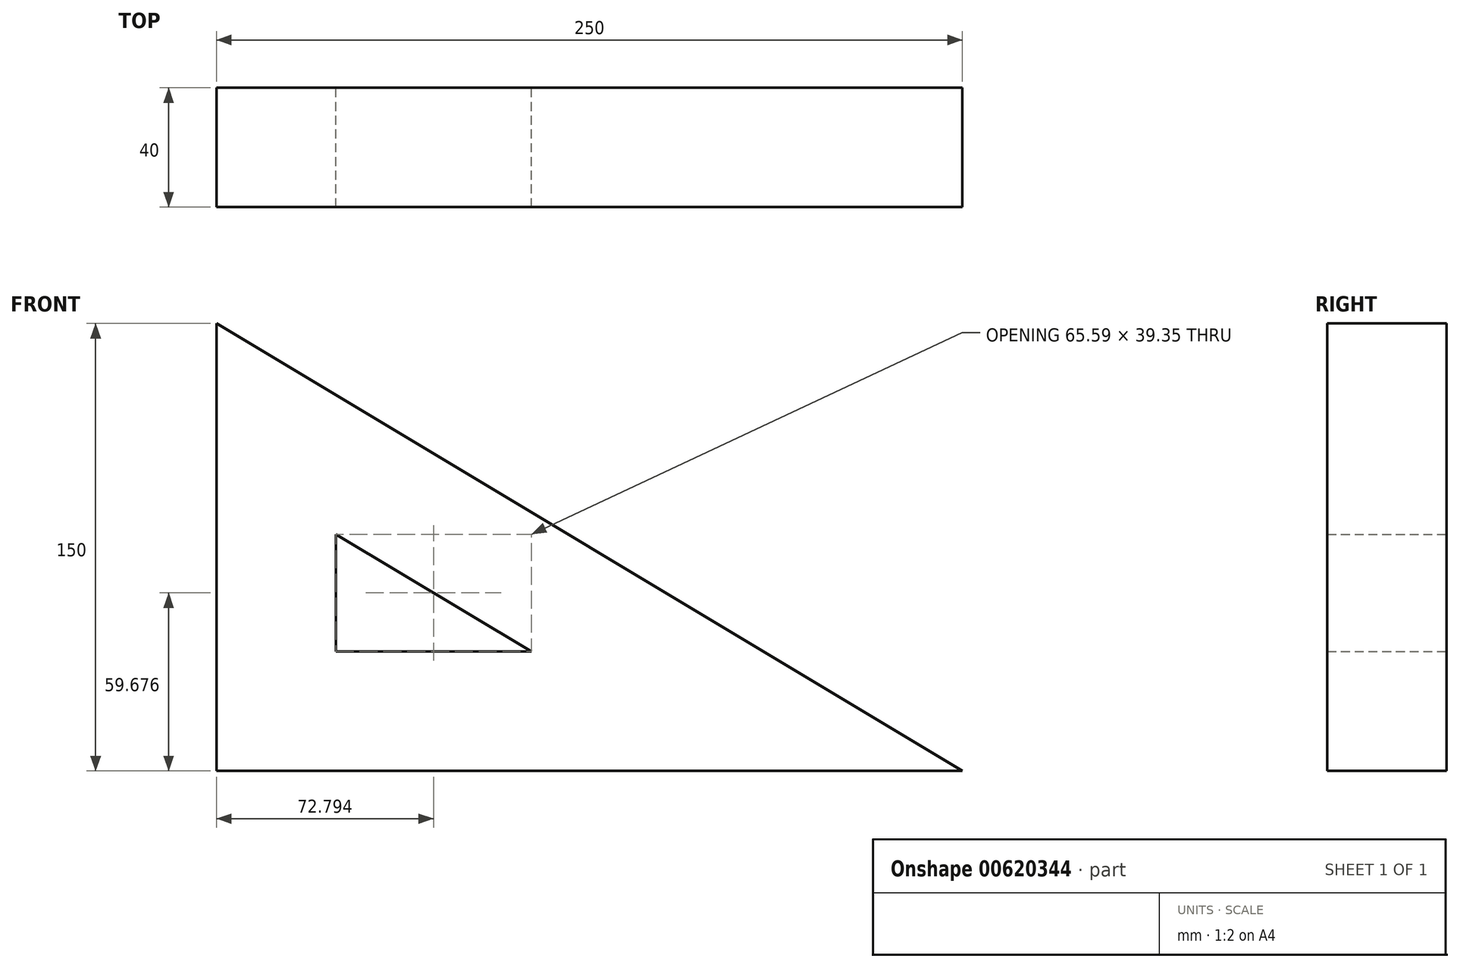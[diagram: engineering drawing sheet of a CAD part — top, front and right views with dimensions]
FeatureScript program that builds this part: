
annotation { "Feature Type Name" : "Feature", "Feature Type Description" : "" }
export const myFeature = defineFeature(function(context is Context, id is Id, definition is map)
    precondition{}
    {
        {
            var Q0;
            Q0=qCreatedBy(makeId("Front.planeOp"),FACE);
            var sketch = newSketch(context, id + "F0", { "sketchPlane" : qUnion([Q0])});
            skLineSegment(sketch, "E0", {"start": v(0, 0) * mm, "end": v(0, 150) * mm});
            skLineSegment(sketch, "E1", {"start": v(0, 150) * mm, "end": v(250, 0) * mm});
            skLineSegment(sketch, "E2", {"start": v(250, 0) * mm, "end": v(0, 0) * mm});
            skLineSegment(sketch, "E3", {"start": v(40, 40) * mm, "end": v(40, 79.35) * mm});
            skLineSegment(sketch, "E4", {"start": v(40, 79.35) * mm, "end": v(105.59, 40) * mm});
            skLineSegment(sketch, "E5", {"start": v(105.59, 40) * mm, "end": v(40, 40) * mm});
            skSolve(sketch);
        }
        {
            var Q0;
            {var subQ0=sQuery(id+"F0.wireOp",EDGE,"bshKKFRv-djKj-atzY-SsEw-5QaEbBUO7jPM");Q0=makeQuery(id+"F0.imprint","IMPRINT",FACE,{"disambiguationData":[TD([[makeQuery(id+"F0.imprint","IMPRINT",EDGE,{"derivedFrom":subQ0}),-1.0]])]});}
            var Q1;
            Q1=makeQuery(id+"F0.imprint","IMPRINT",FACE,{"disambiguationData":[TD([[makeQuery(id+"F0.imprint","IMPRINT",EDGE,{"derivedFrom":sQuery(id+"F0.wireOp",EDGE,"E0")}),-1.0]])]});
            extrude(context, id + "F1", {"entities" : qUnion([Q0, Q1]), "depth" : 40 * mm, "offsetDistance" : 25 * mm});
        }
    });
